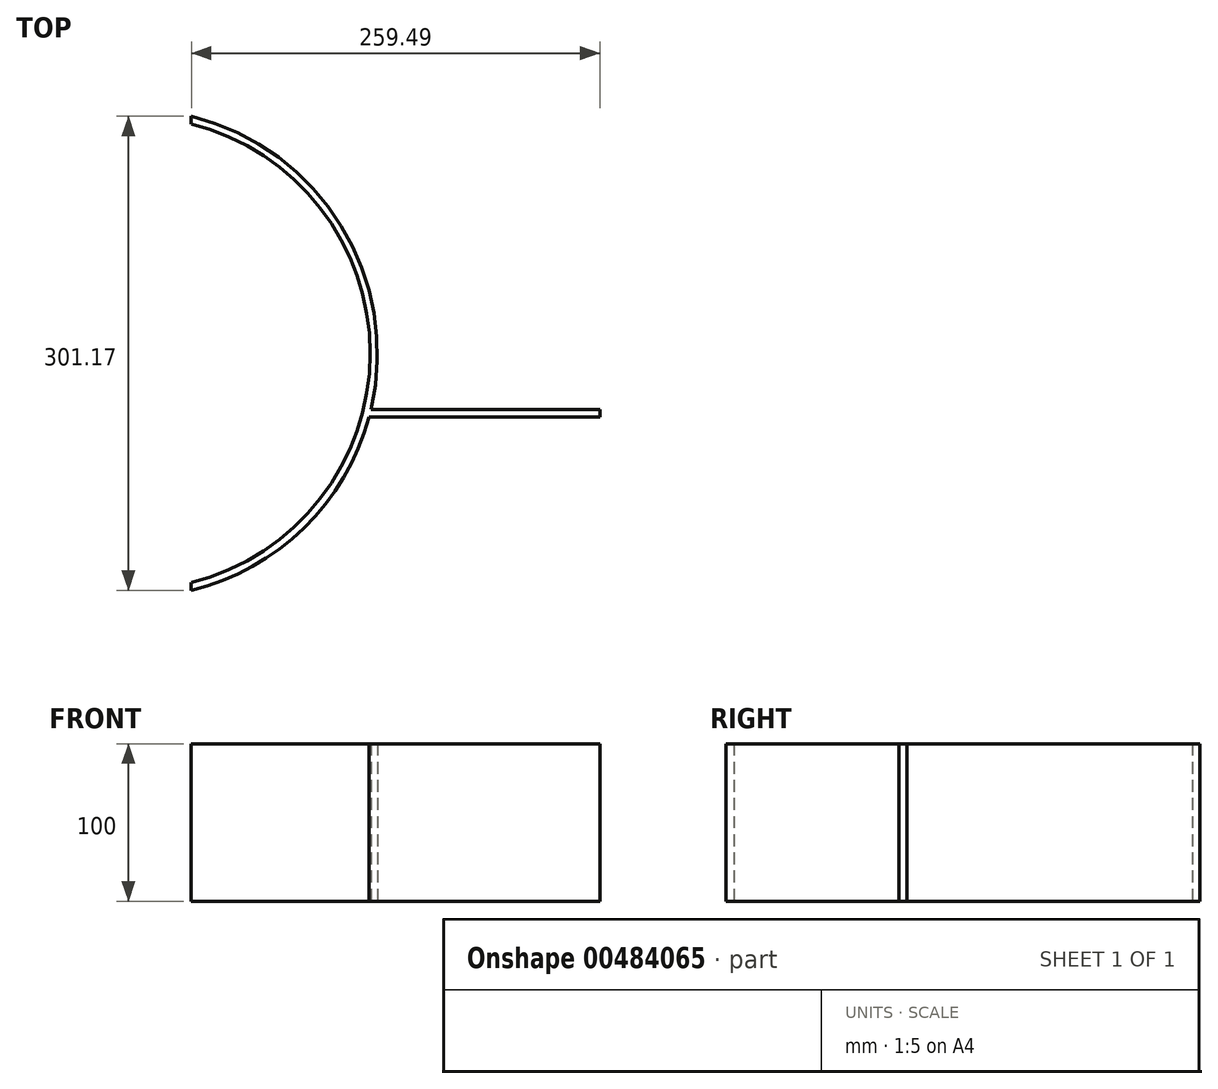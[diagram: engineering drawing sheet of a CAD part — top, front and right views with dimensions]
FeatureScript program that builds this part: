
annotation { "Feature Type Name" : "Feature", "Feature Type Description" : "" }
export const myFeature = defineFeature(function(context is Context, id is Id, definition is map)
    precondition{}
    {
        {
            var Q0;
            Q0=qCreatedBy(makeId("Top.planeOp"),FACE);
            var sketch = newSketch(context, id + "F0", { "sketchPlane" : qUnion([Q0])});
            skLineSegment(sketch, "E0", {"start": v(299.47, -34.57) * mm, "end": v(299.47, -29.57) * mm});
            skArc(sketch, "E1", {"start": v(39.98, -144.57) * mm, "mid": v(111.46, -105.01) * mm, "end": v(152.84, -34.57) * mm});
            skArc(sketch, "E2", {"start": v(154.1, -29.57) * mm, "mid": v(135.12, 86.86) * mm, "end": v(39.98, 156.6) * mm});
            skArc(sketch, "E3", {"start": v(39.98, -139.57) * mm, "mid": v(153.55, 6.02) * mm, "end": v(39.98, 151.6) * mm});
            skLineSegment(sketch, "E4", {"start": v(39.98, -144.57) * mm, "end": v(39.98, -139.57) * mm});
            skLineSegment(sketch, "E5", {"start": v(39.98, 151.6) * mm, "end": v(39.98, 156.6) * mm});
            skLineSegment(sketch, "E6", {"start": v(152.84, -34.57) * mm, "end": v(299.47, -34.57) * mm});
            skLineSegment(sketch, "E7", {"start": v(299.47, -29.57) * mm, "end": v(154.1, -29.57) * mm});
            skSolve(sketch);
        }
        {
            var Q0;
            Q0=qSketchRegion(id+"F0",true);
            extrude(context, id + "F1", {"entities" : qUnion([Q0]), "depth" : 100 * mm});
        }
    });
